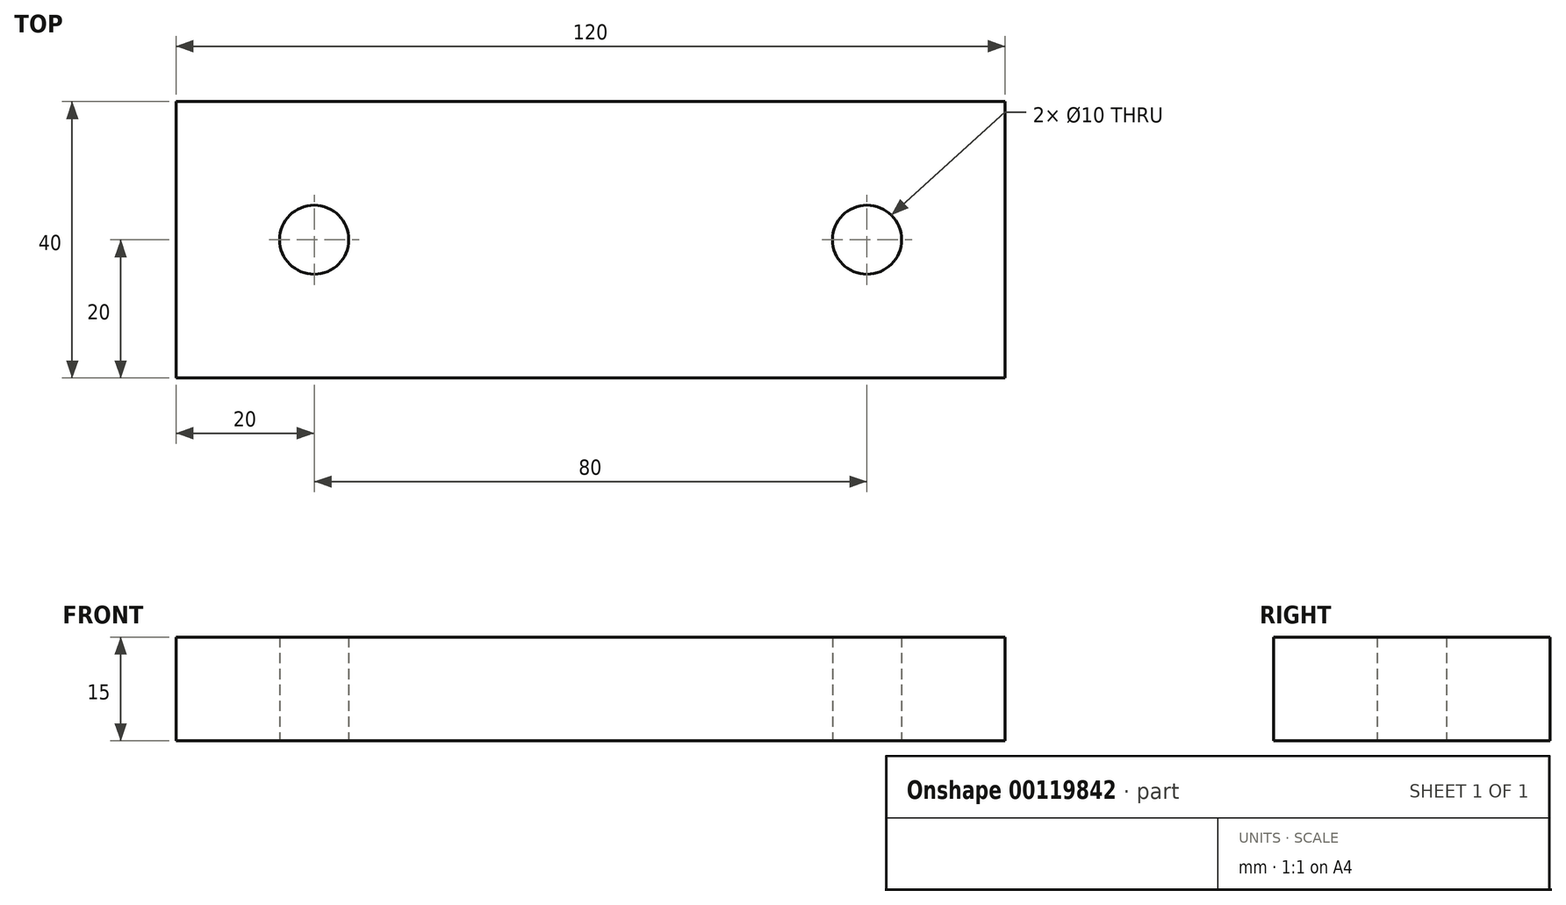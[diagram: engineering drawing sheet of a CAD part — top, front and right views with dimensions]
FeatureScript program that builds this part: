
annotation { "Feature Type Name" : "Feature", "Feature Type Description" : "" }
export const myFeature = defineFeature(function(context is Context, id is Id, definition is map)
    precondition{}
    {
        {
            var Q0;
            Q0=qCreatedBy(makeId("Top.planeOp"),FACE);
            var sketch = newSketch(context, id + "F0", { "sketchPlane" : qUnion([Q0])});
            skLineSegment(sketch, "E0.bottom", {"start": v(0, 40) * mm, "end": v(120, 40) * mm});
            skLineSegment(sketch, "E0.top", {"start": v(0, 0) * mm, "end": v(120, 0) * mm});
            skLineSegment(sketch, "E0.left", {"start": v(0, 40) * mm, "end": v(0, 0) * mm});
            skLineSegment(sketch, "E0.right", {"start": v(120, 40) * mm, "end": v(120, 0) * mm});
            skCircle(sketch, "E1", {"center": v(20, 20) * mm, "radius": 5 * mm});
            skCircle(sketch, "E2", {"center": v(100, 20) * mm, "radius": 5 * mm});
            skLineSegment(sketch, "E3", {"start": v(0, 20) * mm, "end": v(154.37, 20) * mm, "construction": true});
            skSolve(sketch);
        }
        {
            var Q0;
            Q0=makeQuery(id+"F0.imprint","IMPRINT",FACE,{"disambiguationData":[TD([[makeQuery(id+"F0.imprint","IMPRINT",EDGE,{"derivedFrom":sQuery(id+"F0.wireOp",EDGE,"E0.bottom")}),-1.0]])]});
            extrude(context, id + "F1", {"entities" : qUnion([Q0]), "depth" : 15 * mm});
        }
    });
